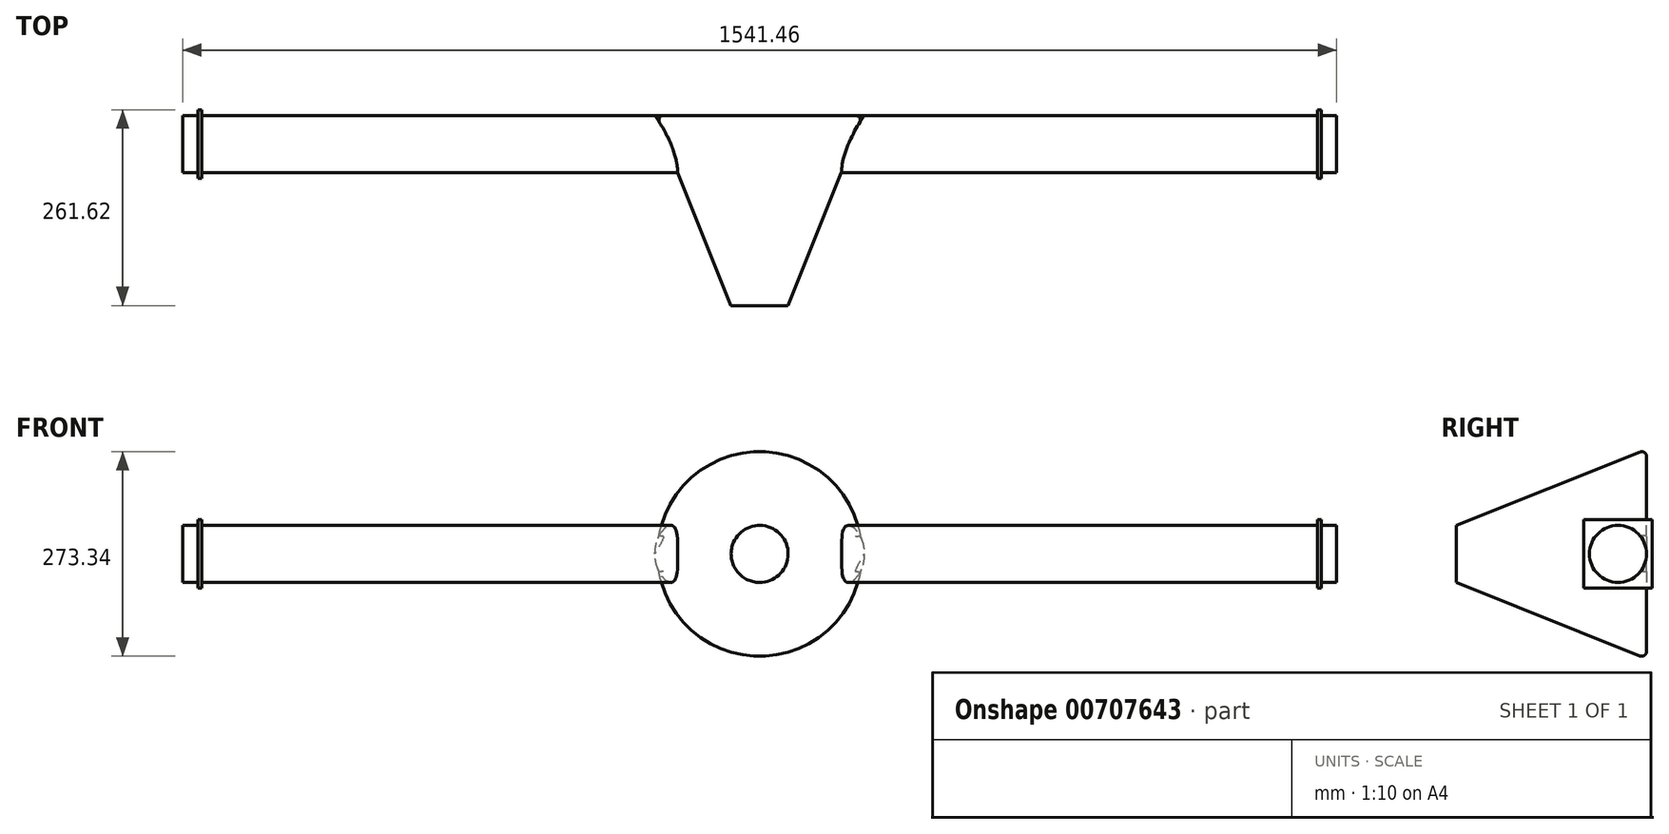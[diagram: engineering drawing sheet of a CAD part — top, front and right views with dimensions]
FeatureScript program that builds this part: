
annotation { "Feature Type Name" : "Feature", "Feature Type Description" : "" }
export const myFeature = defineFeature(function(context is Context, id is Id, definition is map)
    precondition{}
    {
        {
            var Q0;
            Q0=qCreatedBy(makeId("Front.planeOp"),FACE);
            var sketch = newSketch(context, id + "F0", { "sketchPlane" : qUnion([Q0])});
            skCircle(sketch, "E0", {"center": v(0, 0) * mm, "radius": 139.7 * mm});
            skSolve(sketch);
        }
        {
            var Q0;
            Q0=qCreatedBy(makeId("Front.planeOp"),FACE);
            cPlane(context, id + "F1", {"entities" : qUnion([Q0]), "cplaneType" : CPlaneType.OFFSET, "offset" : 254 * mm, "width" : 152.4 * mm, "height" : 152.4 * mm});
        }
        {
            var Q0;
            Q0=qCreatedBy(id+"F1.planeOp",FACE);
            var sketch = newSketch(context, id + "F2", { "sketchPlane" : qUnion([Q0])});
            skCircle(sketch, "E1", {"center": v(0, 0) * mm, "radius": 38.1 * mm});
            skSolve(sketch);
        }
        {
            var Q0;
            Q0=makeQuery(id+"F0.imprint","IMPRINT",FACE,{"disambiguationData":[TD([[makeQuery(id+"F0.imprint","IMPRINT",EDGE,{"derivedFrom":sQuery(id+"F0.wireOp",EDGE,"E0")}),1.0]])]});
            var Q1;
            Q1=makeQuery(id+"F2.imprint","IMPRINT",FACE,{"disambiguationData":[TD([[makeQuery(id+"F2.imprint","IMPRINT",EDGE,{"derivedFrom":sQuery(id+"F2.wireOp",EDGE,"E1")}),1.0]])]});
            loft(context, id + "F3", {"sheetProfilesArray" : [{ "sheetProfileEntities" : qUnion([Q0]) }, { "sheetProfileEntities" : qUnion([Q1]) }]});
        }
        {
            var Q0;
            Q0=qCreatedBy(makeId("Right.planeOp"),FACE);
            var sketch = newSketch(context, id + "F4", { "sketchPlane" : qUnion([Q0])});
            skCircle(sketch, "E2", {"center": v(-38.1, 0) * mm, "radius": 38.1 * mm});
            skSolve(sketch);
        }
        {
            var Q0;
            Q0=qSketchRegion(id+"F4",true);
            extrude(context, id + "F5", {"entities" : qUnion([Q0]), "operationType" : NewBodyOperationType.ADD, "endBound" : BoundingType.SYMMETRIC, "depth" : 1541.46 * mm, "offsetDistance" : 25.4 * mm});
        }
        {
            var Q0;
            Q0=makeQuery(id+"F3.opLoft","MID_CAP_EDGE",EDGE,{"disambiguationData":[OSD([sQuery(id+"F0.wireOp",EDGE,"E0")])],"capPos":0.0});
            fillet(context, id + "F6", {"entities" : qUnion([Q0]), "radius" : 6.35 * mm, "tangentPropagation" : true, "allowEdgeOverflow" : false});
        }
        {
            var Q0;
            Q0=makeQuery(id+"F5.opExtrude","CAP_FACE",FACE,{"disambiguationData":[OSD([sQuery(id+"F4.wireOp",EDGE,"E2")])],"isStart":false});
            cPlane(context, id + "F7", {"entities" : qUnion([Q0]), "cplaneType" : CPlaneType.OFFSET, "offset" : 25.4 * mm, "oppositeDirection" : true, "width" : 152.4 * mm, "height" : 152.4 * mm});
        }
        {
            var Q0;
            Q0=qCreatedBy(id+"F7.planeOp",FACE);
            var sketch = newSketch(context, id + "F8", { "sketchPlane" : qUnion([Q0])});
            skLineSegment(sketch, "E3.bottom", {"start": v(-83.82, 45.72) * mm, "end": v(7.62, 45.72) * mm});
            skLineSegment(sketch, "E3.top", {"start": v(-83.82, -45.72) * mm, "end": v(7.62, -45.72) * mm});
            skLineSegment(sketch, "E3.left", {"start": v(-83.82, 45.72) * mm, "end": v(-83.82, -45.72) * mm});
            skLineSegment(sketch, "E3.right", {"start": v(7.62, 45.72) * mm, "end": v(7.62, -45.72) * mm});
            skSolve(sketch);
        }
        {
            var Q0;
            Q0=qSketchRegion(id+"F8",true);
            extrude(context, id + "F9", {"entities" : qUnion([Q0]), "operationType" : NewBodyOperationType.ADD, "depth" : 5.08 * mm, "offsetDistance" : 25.4 * mm});
        }
        {
            var Q0;
            Q0=makeQuery(id+"F3.opLoft","SWEPT_BODY",BODY,{"disambiguationData":[OSD([makeQuery(id+"F0.imprint","IMPRINT",FACE,{"disambiguationData":[TD([[makeQuery(id+"F0.imprint","IMPRINT",EDGE,{"derivedFrom":sQuery(id+"F0.wireOp",EDGE,"E0")}),1.0]])]}),makeQuery(id+"F2.imprint","IMPRINT",FACE,{"disambiguationData":[TD([[makeQuery(id+"F2.imprint","IMPRINT",EDGE,{"derivedFrom":sQuery(id+"F2.wireOp",EDGE,"E1")}),1.0]])]})])]});
            var Q1;
            Q1=qCreatedBy(makeId("Right.planeOp"),FACE);
            mirror(context, id + "F10", {"operationType" : NewBodyOperationType.ADD, "entities" : qUnion([Q0]), "mirrorPlane" : qUnion([Q1])});
        }
    });
